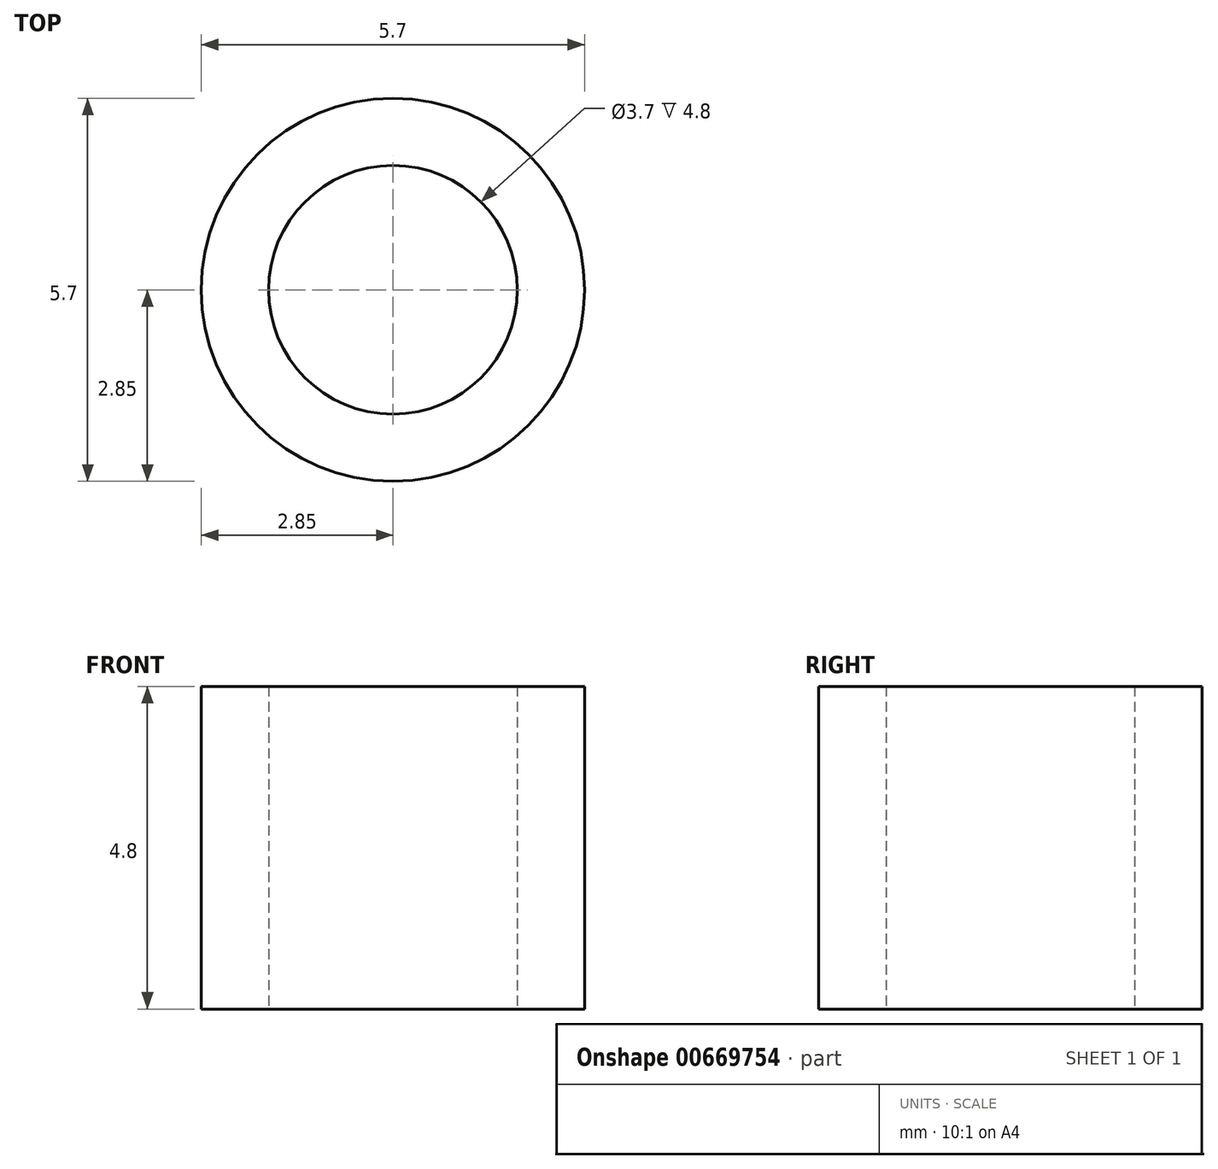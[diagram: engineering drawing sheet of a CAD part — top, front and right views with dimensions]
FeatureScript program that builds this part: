
annotation { "Feature Type Name" : "Feature", "Feature Type Description" : "" }
export const myFeature = defineFeature(function(context is Context, id is Id, definition is map)
    precondition{}
    {
        {
            var Q0;
            Q0=qCreatedBy(makeId("Top.planeOp"),FACE);
            var sketch = newSketch(context, id + "F0", { "sketchPlane" : qUnion([Q0])});
            skCircle(sketch, "E0", {"center": v(0, 0) * mm, "radius": 1.85 * mm});
            skCircle(sketch, "E1", {"center": v(0, 0) * mm, "radius": 2.85 * mm});
            skSolve(sketch);
        }
        {
            var Q0;
            Q0=makeQuery(id+"F0.imprint","IMPRINT",FACE,{"disambiguationData":[TD([[makeQuery(id+"F0.imprint","IMPRINT",EDGE,{"derivedFrom":sQuery(id+"F0.wireOp",EDGE,"E0")}),-1.0]])]});
            var Q1;
            Q1=sQuery(id+"F0.wireOp",EDGE,"E1");
            var Q2;
            Q2=sQuery(id+"F0.wireOp",EDGE,"E0");
            extrude(context, id + "F1", {"entities" : qUnion([Q0]), "surfaceEntities" : qUnion([Q1, Q2]), "depth" : 4.8 * mm, "offsetDistance" : 25 * mm});
        }
    });
